# Revit family: Trägeranbindung IB vertikal, Typ D IV
name_source: partatom
category: HLS-Bauteile
units: mm (PartAtom-declared; Revit-internal decimal feet)

## family parameters
Arbeitsebenenbasiert = Ja
Beim Laden mit Abzugskörper schneiden = Nein
Bemaßung runder Anschluss = Durchmesser verwenden
Beschriftungsausrichtung beibehalten = Nein
Gemeinsam genutzt = Ja
Immer vertikal = Nein
Raumberechnungspunkt = Nein
Teiletyp = Normal

## types (1)
- Trägeranbindung IB vertikal, Typ D IV
    Artikelnummer = 08146104
    EAN = 4250928420091
    Fabrikat = MEFA
    Firma = MEFA Befestigungs- und Montagesysteme GmbH
    Gewicht = 2.05 kg
    Gewicht pro Bauteil = 2.05 kg
    Gewindestangentyp = M16x500
    Klemmweite = 110-360 mm
    Kurztext1 = Trägeranbindung IB C-Profil 45
    Kurztext2 = Typ D IV Klemmdicke 13 - 20 mm
    Material = Stahl
    Materialname = S235
    Mengeneinheit = St
    Oberflaeche = feuerstückverzinkt
    Typ = D IV
    Vorgabe-Ansicht = 1219 mm
    max Klemmdicke = 20 mm  [stored 0.0656168 ft]
    max. Klemmweite = 360 mm
    min. Klemmdicke = 13 mm
    min. Klemmweite = 100 mm  [stored 0.328084 ft]
    vpe = 1

note: [stored X ft] marks values corroborated as IEEE doubles in the binary element streams (Revit-internal decimal feet)

## geometry (parser evidence)
native form markers: Sweep x3
no freeform markers — native parametric forms only
